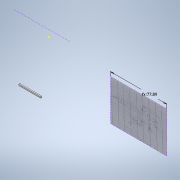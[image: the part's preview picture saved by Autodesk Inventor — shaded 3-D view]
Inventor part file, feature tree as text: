
AUTODESK INVENTOR PART (.ipt)
format: ipt  version: 2022 (Build 260153000, 153)  size: 744,448 bytes
history: native  units: in
note: dims shown in document units (in); Inventor stores cm internally (conversion verified against a paired STEP export)
features: sketch x2, other x2, sheet_metal_op x1
ambient origin geometry x8: Origin, YZ Plane, XZ Plane, XY Plane, X Axis, Y Axis, Z Axis, Center Point
bodies: Solid1 (feature_tree)
feature tree (5):
  sketch  "Sketch1"  dims[d1=3.0666in d2=3.0666in]
  sheet_metal_op  "Face1"
  other  "Image1"
  sketch  "Sketch3"  dims[d3=1.1949in d4=0.0768in d5=0.0591in]
  other  "Plate1"
